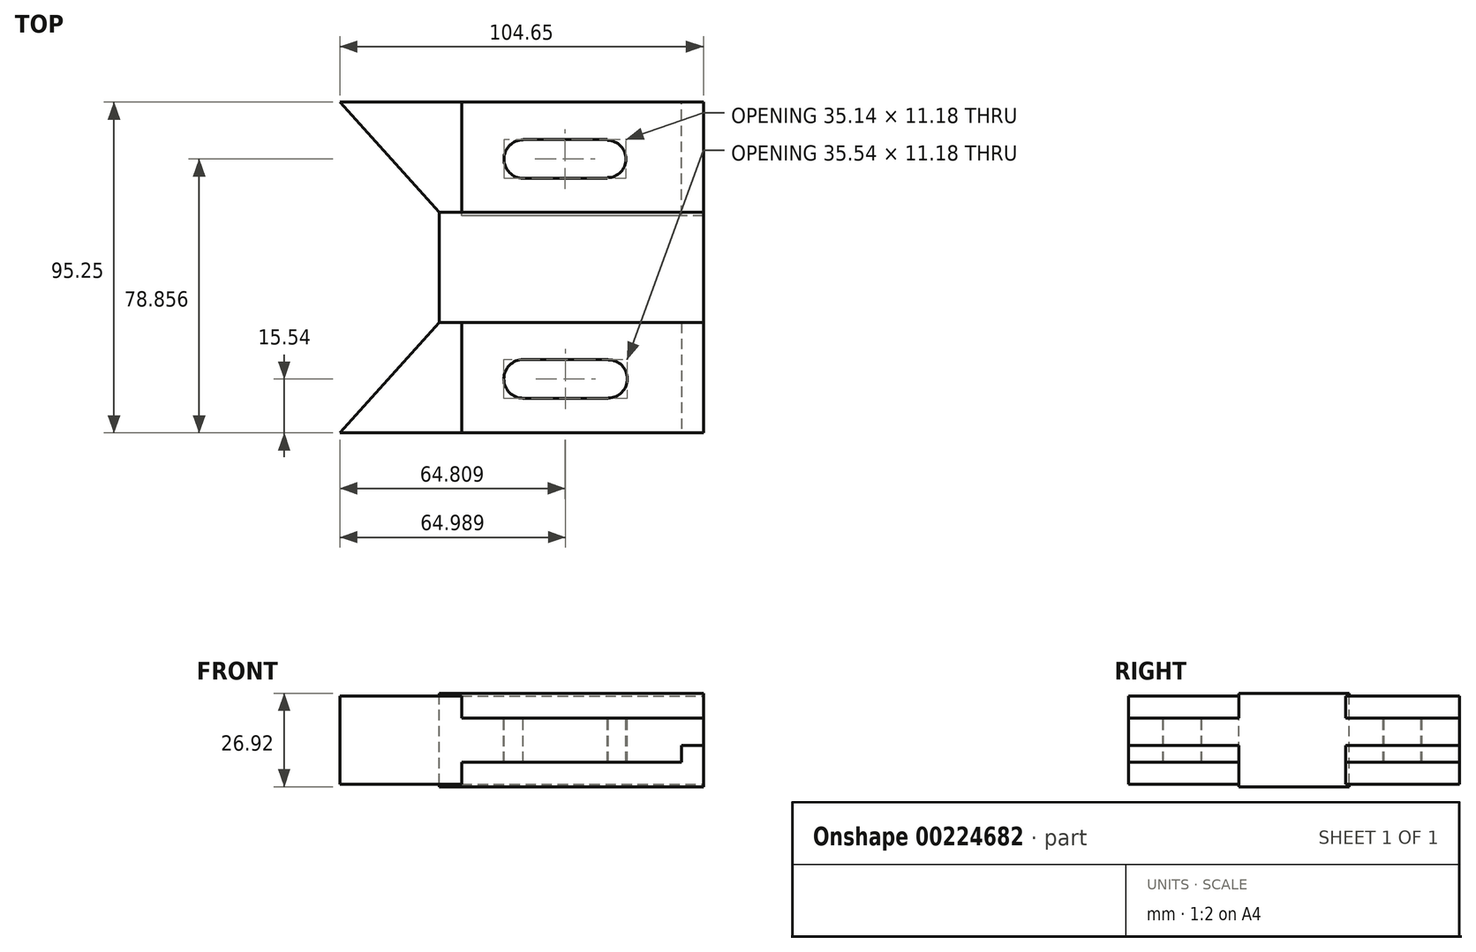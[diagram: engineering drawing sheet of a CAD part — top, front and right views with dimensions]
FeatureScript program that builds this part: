
annotation { "Feature Type Name" : "Feature", "Feature Type Description" : "" }
export const myFeature = defineFeature(function(context is Context, id is Id, definition is map)
    precondition{}
    {
        {
            var Q0;
            Q0=qCreatedBy(makeId("Front.planeOp"),FACE);
            var sketch = newSketch(context, id + "F0", { "sketchPlane" : qUnion([Q0])});
            skLineSegment(sketch, "E0.bottom", {"start": v(0, 0) * mm, "end": v(-75.97, 0) * mm});
            skLineSegment(sketch, "E0.top", {"start": v(0, 26.92) * mm, "end": v(-75.97, 26.92) * mm});
            skLineSegment(sketch, "E0.left", {"start": v(0, 0) * mm, "end": v(0, 26.92) * mm});
            skLineSegment(sketch, "E0.right", {"start": v(-75.97, 0) * mm, "end": v(-75.97, 26.92) * mm});
            skSolve(sketch);
        }
        {
            var Q0;
            Q0 = qSketchRegion(id + "F0", true);
            extrude(context, id + "F1", {"entities" : qUnion([Q0]), "depth" : 31.75 * mm});
        }
        {
            var Q0;
            Q0=makeQuery(id+"F1.opExtrude","SWEPT_FACE",FACE,{"disambiguationData":[OSD([sQuery(id+"F0.wireOp",EDGE,"E0.left")])]});
            var sketch = newSketch(context, id + "F2", { "sketchPlane" : qUnion([Q0])});
            skLineSegment(sketch, "E1.bottom", {"start": v(-31.75, 26.16) * mm, "end": v(-63.5, 26.16) * mm});
            skLineSegment(sketch, "E1.top", {"start": v(-31.75, 0.76) * mm, "end": v(-63.5, 0.76) * mm});
            skLineSegment(sketch, "E1.left", {"start": v(-31.75, 26.16) * mm, "end": v(-31.75, 0.76) * mm});
            skLineSegment(sketch, "E1.right", {"start": v(-63.5, 26.16) * mm, "end": v(-63.5, 0.76) * mm});
            skPoint(sketch, "E1.middle", {"position": v(-47.62, 13.46) * mm});
            skPoint(sketch, "E1.middle.positionSnap0", {"position": v(-31.75, 13.46) * mm});
            skPoint(sketch, "E1.centerSnap0", {"position": v(-31.75, 13.46) * mm});
            skLineSegment(sketch, "E2.bottom", {"start": v(0, 26.16) * mm, "end": v(31.75, 26.16) * mm});
            skLineSegment(sketch, "E2.top", {"start": v(0, 0.76) * mm, "end": v(31.75, 0.76) * mm});
            skLineSegment(sketch, "E2.left", {"start": v(0, 26.16) * mm, "end": v(0, 0.76) * mm});
            skLineSegment(sketch, "E2.right", {"start": v(31.75, 26.16) * mm, "end": v(31.75, 0.76) * mm});
            skPoint(sketch, "E2.middle", {"position": v(15.88, 13.46) * mm});
            skPoint(sketch, "E2.middle.positionSnap0", {"position": v(0, 13.46) * mm});
            skPoint(sketch, "E2.centerSnap0", {"position": v(0, 13.46) * mm});
            skSolve(sketch);
        }
        {
            var Q0;
            Q0 = qSketchRegion(id + "F2", true);
            extrude(context, id + "F3", {"entities" : qUnion([Q0]), "operationType" : NewBodyOperationType.ADD, "oppositeDirection" : true, "depth" : 104.65 * mm});
        }
        {
            var Q0;
            Q0=makeQuery(id+"F3.opExtrude","SWEPT_FACE",FACE,{"disambiguationData":[OSD([sQuery(id+"F2.wireOp",EDGE,"E2.right")])]});
            var sketch = newSketch(context, id + "F4", { "sketchPlane" : qUnion([Q0])});
            skLineSegment(sketch, "E3.bottom", {"start": v(0, 26.16) * mm, "end": v(69.6, 26.16) * mm});
            skLineSegment(sketch, "E3.top", {"start": v(0, 19.81) * mm, "end": v(69.6, 19.81) * mm});
            skLineSegment(sketch, "E3.left", {"start": v(0, 26.16) * mm, "end": v(0, 19.81) * mm});
            skLineSegment(sketch, "E3.right", {"start": v(69.6, 26.16) * mm, "end": v(69.6, 19.81) * mm});
            skLineSegment(sketch, "E4.bottom", {"start": v(0, 0.76) * mm, "end": v(69.6, 0.76) * mm});
            skLineSegment(sketch, "E4.top", {"start": v(0, 7.11) * mm, "end": v(69.6, 7.11) * mm});
            skLineSegment(sketch, "E4.left", {"start": v(0, 0.76) * mm, "end": v(0, 7.11) * mm});
            skLineSegment(sketch, "E4.right", {"start": v(69.6, 0.76) * mm, "end": v(69.6, 7.11) * mm});
            skSolve(sketch);
        }
        {
            var Q0;
            Q0 = qSketchRegion(id + "F4", true);
            extrude(context, id + "F5", {"entities" : qUnion([Q0]), "operationType" : NewBodyOperationType.REMOVE, "oppositeDirection" : true, "depth" : 32.77 * mm});
        }
        {
            var Q0;
            Q0=makeQuery(id+"F3.opExtrude","SWEPT_FACE",FACE,{"disambiguationData":[OSD([sQuery(id+"F2.wireOp",EDGE,"E2.right")])]});
            var sketch = newSketch(context, id + "F6", { "sketchPlane" : qUnion([Q0])});
            skLineSegment(sketch, "E5.bottom", {"start": v(0, 7.11) * mm, "end": v(6.35, 7.11) * mm});
            skLineSegment(sketch, "E5.top", {"start": v(0, 11.94) * mm, "end": v(6.35, 11.94) * mm});
            skLineSegment(sketch, "E5.left", {"start": v(0, 7.11) * mm, "end": v(0, 11.94) * mm});
            skLineSegment(sketch, "E5.right", {"start": v(6.35, 7.11) * mm, "end": v(6.35, 11.94) * mm});
            skSolve(sketch);
        }
        {
            var Q0;
            Q0 = qSketchRegion(id + "F6", true);
            extrude(context, id + "F7", {"entities" : qUnion([Q0]), "operationType" : NewBodyOperationType.ADD, "oppositeDirection" : true, "depth" : 31.75 * mm});
        }
        {
            var Q0;
            Q0 = qSketchRegion(id + "F6", true);
            extrude(context, id + "F8", {"entities" : qUnion([Q0]), "operationType" : NewBodyOperationType.ADD, "oppositeDirection" : true, "depth" : 31.75 * mm});
        }
        {
            var Q0;
            Q0 = qSketchRegion(id + "F6", true);
            extrude(context, id + "F9", {"entities" : qUnion([Q0]), "operationType" : NewBodyOperationType.REMOVE, "oppositeDirection" : true, "depth" : 32 * mm});
        }
        {
            var Q0;
            Q0 = qSketchRegion(id + "F6", true);
            extrude(context, id + "F10", {"entities" : qUnion([Q0]), "operationType" : NewBodyOperationType.ADD, "oppositeDirection" : true, "depth" : 32.77 * mm});
        }
        {
            var Q0;
            Q0 = qSketchRegion(id + "F6", true);
            extrude(context, id + "F11", {"entities" : qUnion([Q0]), "operationType" : NewBodyOperationType.REMOVE, "oppositeDirection" : true, "depth" : 32.77 * mm});
        }
        {
            var Q0;
            Q0=makeQuery(id+"F3.opExtrude","SWEPT_FACE",FACE,{"disambiguationData":[OSD([sQuery(id+"F2.wireOp",EDGE,"E1.right")])]});
            var sketch = newSketch(context, id + "F12", { "sketchPlane" : qUnion([Q0])});
            skLineSegment(sketch, "E6.bottom", {"start": v(0, 0.76) * mm, "end": v(-69.6, 0.76) * mm});
            skLineSegment(sketch, "E6.top", {"start": v(0, 7.11) * mm, "end": v(-69.6, 7.11) * mm});
            skLineSegment(sketch, "E6.left", {"start": v(0, 0.76) * mm, "end": v(0, 7.11) * mm});
            skLineSegment(sketch, "E6.right", {"start": v(-69.6, 0.76) * mm, "end": v(-69.6, 7.11) * mm});
            skLineSegment(sketch, "E7.bottom", {"start": v(0, 26.16) * mm, "end": v(-69.6, 26.16) * mm});
            skLineSegment(sketch, "E7.top", {"start": v(0, 19.81) * mm, "end": v(-69.6, 19.81) * mm});
            skLineSegment(sketch, "E7.left", {"start": v(0, 26.16) * mm, "end": v(0, 19.81) * mm});
            skLineSegment(sketch, "E7.right", {"start": v(-69.6, 26.16) * mm, "end": v(-69.6, 19.81) * mm});
            skSolve(sketch);
        }
        {
            var Q0;
            Q0 = qSketchRegion(id + "F12", true);
            extrude(context, id + "F13", {"entities" : qUnion([Q0]), "operationType" : NewBodyOperationType.REMOVE, "oppositeDirection" : true, "depth" : 31.75 * mm});
        }
        {
            var Q0;
            Q0=makeQuery(id+"F3.opExtrude","SWEPT_FACE",FACE,{"disambiguationData":[OSD([sQuery(id+"F2.wireOp",EDGE,"E1.right")])]});
            var sketch = newSketch(context, id + "F14", { "sketchPlane" : qUnion([Q0])});
            skLineSegment(sketch, "E8.bottom", {"start": v(0, 7.11) * mm, "end": v(-6.35, 7.11) * mm});
            skLineSegment(sketch, "E8.top", {"start": v(0, 11.94) * mm, "end": v(-6.35, 11.94) * mm});
            skLineSegment(sketch, "E8.left", {"start": v(0, 7.11) * mm, "end": v(0, 11.94) * mm});
            skLineSegment(sketch, "E8.right", {"start": v(-6.35, 7.11) * mm, "end": v(-6.35, 11.94) * mm});
            skSolve(sketch);
        }
        {
            var Q0;
            Q0 = qSketchRegion(id + "F14", true);
            extrude(context, id + "F15", {"entities" : qUnion([Q0]), "operationType" : NewBodyOperationType.REMOVE, "oppositeDirection" : true, "depth" : 31.75 * mm});
        }
        {
            var Q0;
            Q0=makeQuery(id+"F5.boolean.opBoolean","COPY",FACE,{"derivedFrom":makeQuery(id+"F5.opExtrude","SWEPT_FACE",FACE,{"disambiguationData":[OSD([sQuery(id+"F4.wireOp",EDGE,"E3.top")])]})});
            var sketch = newSketch(context, id + "F16", { "sketchPlane" : qUnion([Q0])});
            skPoint(sketch, "E9.endSnap0", {"position": v(0, 15.37) * mm});
            skLineSegment(sketch, "E10.bottom", {"start": v(-27.62, 9.77) * mm, "end": v(-51.86, 9.77) * mm});
            skLineSegment(sketch, "E10.top", {"start": v(-27.62, 20.94) * mm, "end": v(-51.86, 20.94) * mm});
            skLineSegment(sketch, "E10.left", {"start": v(-27.62, 9.77) * mm, "end": v(-27.62, 20.94) * mm});
            skLineSegment(sketch, "E10.right", {"start": v(-51.86, 9.77) * mm, "end": v(-51.86, 20.94) * mm});
            skPoint(sketch, "E10.middle", {"position": v(-39.74, 15.36) * mm});
            skCircle(sketch, "E11", {"center": v(-27.62, 15.36) * mm, "radius": 5.35 * mm});
            skCircle(sketch, "E12", {"center": v(-51.86, 15.36) * mm, "radius": 5.55 * mm});
            skSolve(sketch);
        }
        {
            var Q0;
            {var subQ0=sQuery(id+"F16.wireOp",EDGE,"E12");var subQ1=sQuery(id+"F16.wireOp",EDGE,"E10.right");var subQ2=makeQuery(id+"F16.imprint","INTERSECT",VERTEX,{"disambiguationData":[OD(0.0)],"derivedFrom":[subQ1,subQ0]});Q0=makeQuery(id+"F16.imprint","IMPRINT",FACE,{"disambiguationData":[TD([[makeQuery(id+"F16.imprint","IMPRINT",EDGE,{"disambiguationData":[TD([[subQ2,-1.0]])],"derivedFrom":subQ1}),-1.0]])]});}
            var Q1;
            {var subQ0=sQuery(id+"F16.wireOp",EDGE,"E12");var subQ1=sQuery(id+"F16.wireOp",EDGE,"E10.right");var subQ2=makeQuery(id+"F16.imprint","INTERSECT",VERTEX,{"disambiguationData":[OD(0.0)],"derivedFrom":[subQ1,subQ0]});Q1=makeQuery(id+"F16.imprint","IMPRINT",FACE,{"disambiguationData":[TD([[makeQuery(id+"F16.imprint","IMPRINT",EDGE,{"disambiguationData":[TD([[subQ2,-1.0]])],"derivedFrom":subQ1}),1.0]])]});}
            var Q2;
            {var subQ4=sQuery(id+"F16.wireOp",EDGE,"E10.bottom");Q2=makeQuery(id+"F16.imprint","IMPRINT",FACE,{"disambiguationData":[TD([[makeQuery(id+"F16.imprint","IMPRINT",EDGE,{"derivedFrom":subQ4}),-1.0]])]});}
            var Q3;
            {var subQ0=sQuery(id+"F16.wireOp",EDGE,"E11");var subQ1=sQuery(id+"F16.wireOp",EDGE,"E10.left");var subQ2=makeQuery(id+"F16.imprint","INTERSECT",VERTEX,{"disambiguationData":[OD(0.0)],"derivedFrom":[subQ1,subQ0]});Q3=makeQuery(id+"F16.imprint","IMPRINT",FACE,{"disambiguationData":[TD([[makeQuery(id+"F16.imprint","IMPRINT",EDGE,{"disambiguationData":[TD([[subQ2,-1.0]])],"derivedFrom":subQ1}),1.0]])]});}
            var Q4;
            {var subQ0=sQuery(id+"F16.wireOp",EDGE,"E11");var subQ1=sQuery(id+"F16.wireOp",EDGE,"E10.left");var subQ2=makeQuery(id+"F16.imprint","INTERSECT",VERTEX,{"disambiguationData":[OD(0.0)],"derivedFrom":[subQ1,subQ0]});Q4=makeQuery(id+"F16.imprint","IMPRINT",FACE,{"disambiguationData":[TD([[makeQuery(id+"F16.imprint","IMPRINT",EDGE,{"disambiguationData":[TD([[subQ2,-1.0]])],"derivedFrom":subQ1}),-1.0]])]});}
            extrude(context, id + "F17", {"entities" : qUnion([Q0, Q1, Q2, Q3, Q4]), "operationType" : NewBodyOperationType.REMOVE, "endBound" : BoundingType.THROUGH_ALL, "oppositeDirection" : true, "depth" : 25.4 * mm});
        }
        {
            var Q0;
            Q0=makeQuery(id+"F13.boolean.opBoolean","COPY",FACE,{"derivedFrom":makeQuery(id+"F13.opExtrude","SWEPT_FACE",FACE,{"disambiguationData":[OSD([sQuery(id+"F12.wireOp",EDGE,"E7.top")])]})});
            var sketch = newSketch(context, id + "F18", { "sketchPlane" : qUnion([Q0])});
            skLineSegment(sketch, "E13.bottom", {"start": v(-27.39, -53.55) * mm, "end": v(-51.86, -53.55) * mm});
            skLineSegment(sketch, "E13.top", {"start": v(-27.39, -42.37) * mm, "end": v(-51.86, -42.37) * mm});
            skLineSegment(sketch, "E13.left", {"start": v(-27.39, -53.55) * mm, "end": v(-27.39, -42.37) * mm});
            skLineSegment(sketch, "E13.right", {"start": v(-51.86, -53.55) * mm, "end": v(-51.86, -42.37) * mm});
            skPoint(sketch, "E13.middle", {"position": v(-39.62, -47.96) * mm});
            skCircle(sketch, "E14", {"center": v(-27.39, -47.96) * mm, "radius": 5.5 * mm});
            skCircle(sketch, "E15", {"center": v(-51.86, -47.96) * mm, "radius": 5.57 * mm});
            skLineSegment(sketch, "E16", {"start": v(-39.62, -47.96) * mm, "end": v(-39.62, -47.96) * mm});
            skSolve(sketch);
        }
        {
            var Q0;
            Q0 = qSketchRegion(id + "F18", true);
            extrude(context, id + "F19", {"entities" : qUnion([Q0]), "operationType" : NewBodyOperationType.REMOVE, "endBound" : BoundingType.THROUGH_ALL, "oppositeDirection" : true, "depth" : 25.4 * mm});
        }
        {
            var Q0;
            Q0=makeQuery(id+"F3.opExtrude","SWEPT_FACE",FACE,{"disambiguationData":[OSD([sQuery(id+"F2.wireOp",EDGE,"E1.bottom")])]});
            var sketch = newSketch(context, id + "F20", { "sketchPlane" : qUnion([Q0])});
            skLineSegment(sketch, "E17", {"start": v(-104.65, -63.5) * mm, "end": v(-75.97, -31.75) * mm});
            skSolve(sketch);
        }
        {
            var Q0;
            Q0=makeQuery(id+"F20.imprint","IMPRINT",FACE,{"disambiguationData":[TD([[makeQuery(id+"F20.imprint","IMPRINT",EDGE,{"derivedFrom":sQuery(id+"F20.wireOp",EDGE,"E17")}),1.0]])]});
            extrude(context, id + "F21", {"entities" : qUnion([Q0]), "operationType" : NewBodyOperationType.REMOVE, "endBound" : BoundingType.THROUGH_ALL, "oppositeDirection" : true, "depth" : 25.4 * mm});
        }
        {
            var Q0;
            Q0=makeQuery(id+"F3.opExtrude","SWEPT_FACE",FACE,{"disambiguationData":[OSD([sQuery(id+"F2.wireOp",EDGE,"E2.bottom")])]});
            var sketch = newSketch(context, id + "F22", { "sketchPlane" : qUnion([Q0])});
            skLineSegment(sketch, "E18", {"start": v(-75.97, 0) * mm, "end": v(-104.65, 31.75) * mm});
            skSolve(sketch);
        }
        {
            var Q0;
            Q0 = qSketchRegion(id + "F22", true);
            var Q1;
            Q1=makeQuery(id+"F22.imprint","IMPRINT",FACE,{"disambiguationData":[TD([[makeQuery(id+"F22.imprint","IMPRINT",EDGE,{"derivedFrom":sQuery(id+"F22.wireOp",EDGE,"E18")}),1.0]])]});
            extrude(context, id + "F23", {"entities" : qUnion([Q0, Q1]), "operationType" : NewBodyOperationType.REMOVE, "endBound" : BoundingType.THROUGH_ALL, "oppositeDirection" : true, "depth" : 25.4 * mm});
        }
    });
